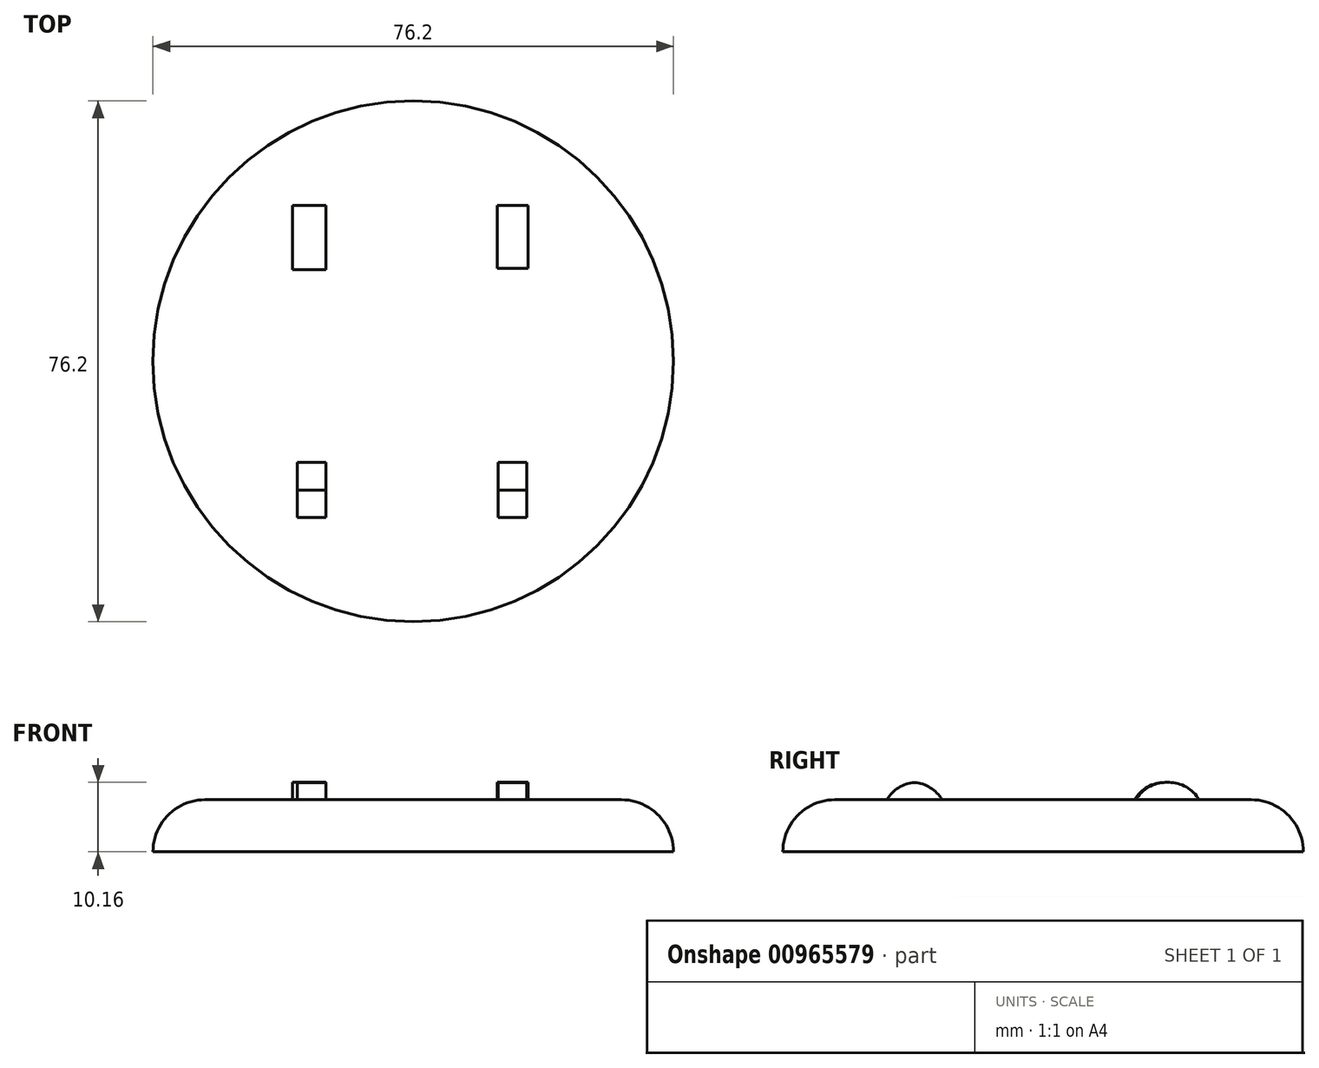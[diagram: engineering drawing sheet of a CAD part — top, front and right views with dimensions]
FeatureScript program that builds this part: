
annotation { "Feature Type Name" : "Feature", "Feature Type Description" : "" }
export const myFeature = defineFeature(function(context is Context, id is Id, definition is map)
    precondition{}
    {
        {
            var Q0;
            Q0=qCreatedBy(makeId("Top.planeOp"),FACE);
            var sketch = newSketch(context, id + "F0", { "sketchPlane" : qUnion([Q0])});
            skCircle(sketch, "E0", {"center": v(0, 0) * mm, "radius": 38.1 * mm});
            skLineSegment(sketch, "E1.bottom", {"start": v(-16.98, -22.84) * mm, "end": v(-12.8, -22.84) * mm});
            skLineSegment(sketch, "E1.top", {"start": v(-16.98, -14.8) * mm, "end": v(-12.8, -14.8) * mm});
            skLineSegment(sketch, "E1.left", {"start": v(-16.98, -22.84) * mm, "end": v(-16.98, -14.8) * mm});
            skLineSegment(sketch, "E1.right", {"start": v(-12.8, -22.84) * mm, "end": v(-12.8, -14.8) * mm});
            skLineSegment(sketch, "E2.bottom", {"start": v(12.45, -22.84) * mm, "end": v(16.63, -22.84) * mm});
            skLineSegment(sketch, "E2.top", {"start": v(12.45, -14.8) * mm, "end": v(16.63, -14.8) * mm});
            skLineSegment(sketch, "E2.left", {"start": v(12.45, -22.84) * mm, "end": v(12.45, -14.8) * mm});
            skLineSegment(sketch, "E2.right", {"start": v(16.63, -22.84) * mm, "end": v(16.63, -14.8) * mm});
            skLineSegment(sketch, "E3.bottom", {"start": v(-17.67, 22.84) * mm, "end": v(-12.8, 22.84) * mm});
            skLineSegment(sketch, "E3.top", {"start": v(-17.67, 13.4) * mm, "end": v(-12.8, 13.4) * mm});
            skLineSegment(sketch, "E3.left", {"start": v(-17.67, 22.84) * mm, "end": v(-17.67, 13.4) * mm});
            skLineSegment(sketch, "E3.right", {"start": v(-12.8, 22.84) * mm, "end": v(-12.8, 13.4) * mm});
            skLineSegment(sketch, "E4.bottom", {"start": v(16.8, 22.84) * mm, "end": v(12.28, 22.84) * mm});
            skLineSegment(sketch, "E4.top", {"start": v(16.8, 13.58) * mm, "end": v(12.28, 13.58) * mm});
            skLineSegment(sketch, "E4.left", {"start": v(16.8, 22.84) * mm, "end": v(16.8, 13.58) * mm});
            skLineSegment(sketch, "E4.right", {"start": v(12.28, 22.84) * mm, "end": v(12.28, 13.58) * mm});
            skSolve(sketch);
        }
        {
            var Q0;
            Q0 = qSketchRegion(id + "F0", true);
            extrude(context, id + "F1", {"entities" : qUnion([Q0]), "depth" : 7.62 * mm, "offsetDistance" : 25.4 * mm});
        }
        {
            var Q0;
            Q0=makeQuery(id+"F1.opExtrude","CAP_EDGE",EDGE,{"disambiguationData":[OSD([sQuery(id+"F0.wireOp",EDGE,"E0")])],"isStart":false});
            fillet(context, id + "F2", {"entities" : qUnion([Q0]), "radius" : 7.62 * mm, "tangentPropagation" : true, "allowEdgeOverflow" : false});
        }
        {
            var Q0;
            Q0=makeQuery(id+"F0.imprint","IMPRINT",FACE,{"disambiguationData":[TD([[makeQuery(id+"F0.imprint","IMPRINT",EDGE,{"derivedFrom":sQuery(id+"F0.wireOp",EDGE,"E3.bottom")}),-1.0]])]});
            var Q1;
            Q1=makeQuery(id+"F0.imprint","IMPRINT",FACE,{"disambiguationData":[TD([[makeQuery(id+"F0.imprint","IMPRINT",EDGE,{"derivedFrom":sQuery(id+"F0.wireOp",EDGE,"E4.bottom")}),1.0]])]});
            var Q2;
            Q2=makeQuery(id+"F0.imprint","IMPRINT",FACE,{"disambiguationData":[TD([[makeQuery(id+"F0.imprint","IMPRINT",EDGE,{"derivedFrom":sQuery(id+"F0.wireOp",EDGE,"E2.bottom")}),1.0]])]});
            var Q3;
            Q3=makeQuery(id+"F0.imprint","IMPRINT",FACE,{"disambiguationData":[TD([[makeQuery(id+"F0.imprint","IMPRINT",EDGE,{"derivedFrom":sQuery(id+"F0.wireOp",EDGE,"E1.bottom")}),1.0]])]});
            extrude(context, id + "F3", {"entities" : qUnion([Q0, Q1, Q2, Q3]), "operationType" : NewBodyOperationType.ADD, "depth" : 10.16 * mm, "offsetDistance" : 25.4 * mm});
        }
        {
            var Q0;
            Q0=makeQuery(id+"F3.opExtrude","CAP_EDGE",EDGE,{"disambiguationData":[OSD([sQuery(id+"F0.wireOp",EDGE,"E1.bottom")])],"isStart":false});
            var Q1;
            Q1=makeQuery(id+"F3.opExtrude","CAP_EDGE",EDGE,{"disambiguationData":[OSD([sQuery(id+"F0.wireOp",EDGE,"E2.bottom")])],"isStart":false});
            var Q2;
            Q2=makeQuery(id+"F3.opExtrude","CAP_EDGE",EDGE,{"disambiguationData":[OSD([sQuery(id+"F0.wireOp",EDGE,"E4.top")])],"isStart":false});
            var Q3;
            Q3=makeQuery(id+"F3.opExtrude","CAP_EDGE",EDGE,{"disambiguationData":[OSD([sQuery(id+"F0.wireOp",EDGE,"E3.top")])],"isStart":false});
            var Q4;
            Q4=makeQuery(id+"F3.opExtrude","CAP_EDGE",EDGE,{"disambiguationData":[OSD([sQuery(id+"F0.wireOp",EDGE,"E1.top")])],"isStart":false});
            var Q5;
            Q5=makeQuery(id+"F3.opExtrude","CAP_EDGE",EDGE,{"disambiguationData":[OSD([sQuery(id+"F0.wireOp",EDGE,"E2.top")])],"isStart":false});
            var Q6;
            Q6=makeQuery(id+"F3.opExtrude","CAP_EDGE",EDGE,{"disambiguationData":[OSD([sQuery(id+"F0.wireOp",EDGE,"E4.bottom")])],"isStart":false});
            var Q7;
            Q7=makeQuery(id+"F3.opExtrude","CAP_EDGE",EDGE,{"disambiguationData":[OSD([sQuery(id+"F0.wireOp",EDGE,"E3.bottom")])],"isStart":false});
            fillet(context, id + "F4", {"entities" : qUnion([Q0, Q1, Q2, Q3, Q4, Q5, Q6, Q7]), "radius" : 5.08 * mm, "tangentPropagation" : true, "allowEdgeOverflow" : false});
        }
    });
